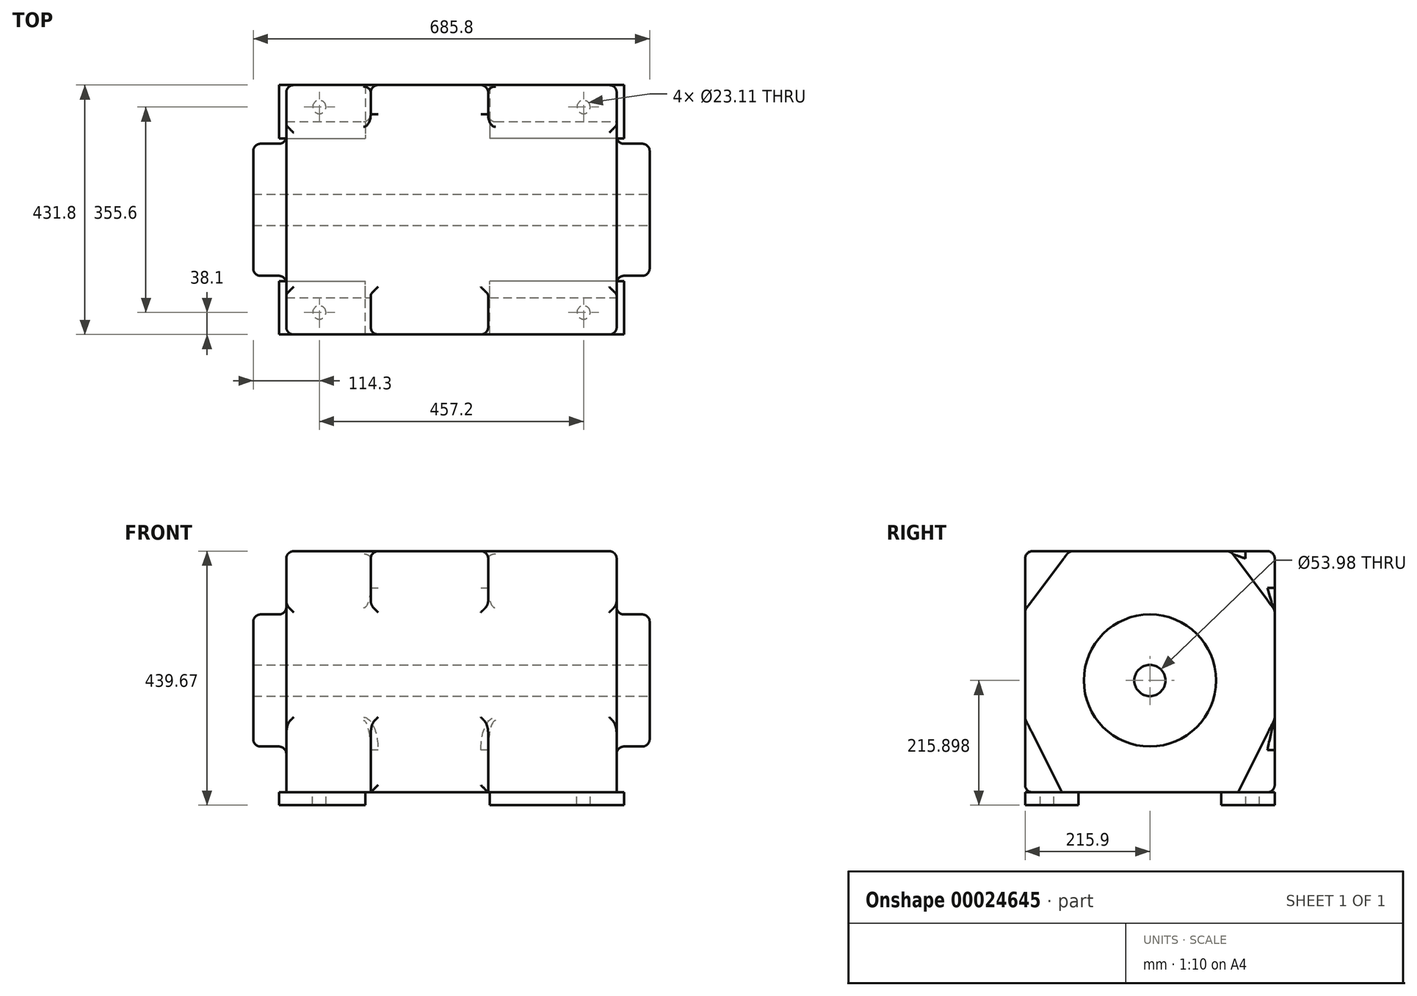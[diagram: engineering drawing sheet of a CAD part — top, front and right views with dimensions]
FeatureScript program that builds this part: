
annotation { "Feature Type Name" : "Feature", "Feature Type Description" : "" }
export const myFeature = defineFeature(function(context is Context, id is Id, definition is map)
    precondition{}
    {
        {
            var Q0;
            Q0=qCreatedBy(makeId("Top.planeOp"),FACE);
            var sketch = newSketch(context, id + "F0", { "sketchPlane" : qUnion([Q0])});
            skLineSegment(sketch, "E0", {"start": v(0, 97.33) * mm, "end": v(0, -215.9) * mm, "construction": true});
            skLineSegment(sketch, "E1", {"start": v(-109.5, 0) * mm, "end": v(101.39, 0) * mm, "construction": true});
            skLineSegment(sketch, "E2.0", {"start": v(-298.45, 215.9) * mm, "end": v(-298.45, -215.9) * mm, "construction": true});
            skLineSegment(sketch, "E3.0", {"start": v(-298.45, -215.9) * mm, "end": v(298.45, -215.9) * mm, "construction": true});
            skLineSegment(sketch, "E4.MirrorCS", {"start": v(298.45, 215.9) * mm, "end": v(298.45, -215.9) * mm, "construction": true});
            skLineSegment(sketch, "E5.MirrorCS", {"start": v(-298.45, 215.9) * mm, "end": v(298.45, 215.9) * mm, "construction": true});
            skPoint(sketch, "E6.orphan", {"position": v(-298.45, 97.33) * mm});
            skPoint(sketch, "E7.orphan", {"position": v(298.45, 97.33) * mm});
            skLineSegment(sketch, "E8.bottom", {"start": v(-298.45, -215.9) * mm, "end": v(-149.1, -215.9) * mm});
            skLineSegment(sketch, "E8.top", {"start": v(-298.45, -123.7) * mm, "end": v(-149.1, -123.7) * mm});
            skLineSegment(sketch, "E8.left", {"start": v(-298.45, -215.9) * mm, "end": v(-298.45, -123.7) * mm});
            skLineSegment(sketch, "E8.right", {"start": v(-149.1, -215.9) * mm, "end": v(-149.1, -123.7) * mm});
            skLineSegment(sketch, "E9.bottom", {"start": v(298.45, -215.9) * mm, "end": v(66.55, -215.9) * mm});
            skLineSegment(sketch, "E9.top", {"start": v(298.45, -123.7) * mm, "end": v(66.55, -123.7) * mm});
            skLineSegment(sketch, "E9.left", {"start": v(298.45, -215.9) * mm, "end": v(298.45, -123.7) * mm});
            skLineSegment(sketch, "E9.right", {"start": v(66.55, -215.9) * mm, "end": v(66.55, -123.7) * mm});
            skLineSegment(sketch, "E10.0", {"start": v(-228.6, 97.33) * mm, "end": v(-228.6, -215.9) * mm, "construction": true});
            skLineSegment(sketch, "E11.0", {"start": v(-228.6, -177.8) * mm, "end": v(101.39, -177.8) * mm, "construction": true});
            skCircle(sketch, "E12", {"center": v(-228.6, -177.8) * mm, "radius": 11.56 * mm});
            skCircle(sketch, "E13.MirrorC", {"center": v(228.6, -177.8) * mm, "radius": 11.56 * mm});
            skCircle(sketch, "E14.MirrorC", {"center": v(-228.6, 177.8) * mm, "radius": 11.56 * mm});
            skLineSegment(sketch, "E15.MirrorCS", {"start": v(-298.45, 123.7) * mm, "end": v(-149.1, 123.7) * mm});
            skLineSegment(sketch, "E16.MirrorCS", {"start": v(-298.45, 215.9) * mm, "end": v(-149.1, 215.9) * mm});
            skLineSegment(sketch, "E17.MirrorCS", {"start": v(-298.45, 215.9) * mm, "end": v(-298.45, 123.7) * mm});
            skLineSegment(sketch, "E18.MirrorCS", {"start": v(-149.1, 215.9) * mm, "end": v(-149.1, 123.7) * mm});
            skLineSegment(sketch, "E19.MirrorCS", {"start": v(298.45, 215.9) * mm, "end": v(298.45, 123.7) * mm});
            skLineSegment(sketch, "E20.MirrorCS", {"start": v(-228.6, 177.8) * mm, "end": v(101.39, 177.8) * mm, "construction": true});
            skLineSegment(sketch, "E21.MirrorCS", {"start": v(-298.45, 215.9) * mm, "end": v(298.45, 215.9) * mm});
            skLineSegment(sketch, "E22.MirrorCS", {"start": v(298.45, 123.7) * mm, "end": v(66.55, 123.7) * mm});
            skCircle(sketch, "E23.MirrorC", {"center": v(228.6, 177.8) * mm, "radius": 11.56 * mm});
            skLineSegment(sketch, "E24.MirrorCS", {"start": v(298.45, 215.9) * mm, "end": v(66.55, 215.9) * mm});
            skLineSegment(sketch, "E25.MirrorCS", {"start": v(66.55, 215.9) * mm, "end": v(66.55, 123.7) * mm});
            skSolve(sketch);
        }
        {
            var Q0;
            Q0=qSketchRegion(id+"F0",true);
            extrude(context, id + "F1", {"entities" : qUnion([Q0]), "oppositeDirection" : true, "depth" : 22.35 * mm});
        }
        {
            var Q0;
            Q0=makeQuery(id+"F1.opExtrude","CAP_FACE",FACE,{"disambiguationData":[OSD([sQuery(id+"F0.wireOp",EDGE,"E14.MirrorC"),sQuery(id+"F0.wireOp",EDGE,"E15.MirrorCS"),sQuery(id+"F0.wireOp",EDGE,"E17.MirrorCS"),sQuery(id+"F0.wireOp",EDGE,"E18.MirrorCS"),sQuery(id+"F0.wireOp",EDGE,"E21.MirrorCS")])],"isStart":true});
            var sketch = newSketch(context, id + "F2", { "sketchPlane" : qUnion([Q0])});
            skLineSegment(sketch, "E26.bottom", {"start": v(-285.75, 139.7) * mm, "end": v(285.75, 139.7) * mm});
            skLineSegment(sketch, "E26.top", {"start": v(-285.75, -139.7) * mm, "end": v(285.75, -139.7) * mm});
            skLineSegment(sketch, "E26.left", {"start": v(-285.75, 139.7) * mm, "end": v(-285.75, -139.7) * mm});
            skLineSegment(sketch, "E26.right", {"start": v(285.75, 139.7) * mm, "end": v(285.75, -139.7) * mm});
            skSolve(sketch);
        }
        {
            var Q0;
            Q0=qSketchRegion(id+"F2",true);
            extrude(context, id + "F3", {"entities" : qUnion([Q0]), "operationType" : NewBodyOperationType.ADD, "depth" : 417.32 * mm});
        }
        {
            var Q0;
            Q0=makeQuery(id+"F3.opExtrude","SWEPT_FACE",FACE,{"disambiguationData":[OSD([sQuery(id+"F2.wireOp",EDGE,"E26.right")])]});
            var sketch = newSketch(context, id + "F4", { "sketchPlane" : qUnion([Q0])});
            skLineSegment(sketch, "E27.0", {"start": v(-215.9, 0) * mm, "end": v(-123.7, 0) * mm, "construction": true});
            skLineSegment(sketch, "E28.0", {"start": v(215.9, 0) * mm, "end": v(123.7, 0) * mm, "construction": true});
            skLineSegment(sketch, "E29.0", {"start": v(139.7, 417.32) * mm, "end": v(-139.7, 417.32) * mm, "construction": true});
            skLineSegment(sketch, "E30", {"start": v(215.9, 0) * mm, "end": v(215.9, 417.32) * mm, "construction": true});
            skLineSegment(sketch, "E31.bottom", {"start": v(0, 0) * mm, "end": v(215.9, 0) * mm});
            skLineSegment(sketch, "E31.top", {"start": v(0, 417.32) * mm, "end": v(139.7, 417.32) * mm});
            skLineSegment(sketch, "E31.left", {"start": v(0, 0) * mm, "end": v(0, 417.32) * mm});
            skLineSegment(sketch, "E31.right", {"start": v(215.9, 127) * mm, "end": v(215.9, 315.72) * mm});
            skLineSegment(sketch, "E32", {"start": v(152.4, 0) * mm, "end": v(215.9, 127) * mm});
            skLineSegment(sketch, "E33", {"start": v(139.7, 417.32) * mm, "end": v(215.9, 315.72) * mm});
            skLineSegment(sketch, "E34.MirrorCS", {"start": v(-215.9, 0) * mm, "end": v(-123.7, 0) * mm});
            skLineSegment(sketch, "E35.MirrorCS", {"start": v(-152.4, 0) * mm, "end": v(-215.9, 127) * mm});
            skLineSegment(sketch, "E36.MirrorCS", {"start": v(0, 417.32) * mm, "end": v(-139.7, 417.32) * mm});
            skLineSegment(sketch, "E37.MirrorCS", {"start": v(0, 0) * mm, "end": v(-215.9, 0) * mm});
            skLineSegment(sketch, "E38.MirrorCS", {"start": v(-215.9, 127) * mm, "end": v(-215.9, 315.72) * mm});
            skLineSegment(sketch, "E39.MirrorCS", {"start": v(-215.9, 127) * mm, "end": v(-215.9, 417.32) * mm});
            skLineSegment(sketch, "E40.MirrorCS", {"start": v(-139.7, 417.32) * mm, "end": v(-215.9, 315.72) * mm});
            skSolve(sketch);
        }
        {
            var Q0;
            Q0=qSketchRegion(id+"F4",true);
            var Q1;
            Q1=makeQuery(id+"F3.opExtrude","SWEPT_FACE",FACE,{"disambiguationData":[OSD([sQuery(id+"F2.wireOp",EDGE,"E26.left")])]});
            extrude(context, id + "F5", {"entities" : qUnion([Q0]), "operationType" : NewBodyOperationType.ADD, "endBound" : BoundingType.UP_TO_SURFACE, "oppositeDirection" : true, "endBoundEntityFace" : qUnion([Q1]), "depth" : 25.4 * mm});
        }
        {
            var Q0;
            Q0=qCreatedBy(makeId("Right.planeOp"),FACE);
            var sketch = newSketch(context, id + "F6", { "sketchPlane" : qUnion([Q0])});
            skLineSegment(sketch, "E41.0", {"start": v(-215.9, 0) * mm, "end": v(-123.7, 0) * mm, "construction": true});
            skLineSegment(sketch, "E42.0", {"start": v(215.9, 0) * mm, "end": v(123.7, 0) * mm, "construction": true});
            skLineSegment(sketch, "E43.bottom", {"start": v(215.9, 0) * mm, "end": v(-215.9, 0) * mm, "construction": true});
            skLineSegment(sketch, "E43.top", {"start": v(215.9, 0) * mm, "end": v(-215.9, 0) * mm, "construction": true});
            skLineSegment(sketch, "E43.left", {"start": v(215.9, 0) * mm, "end": v(215.9, 0) * mm});
            skLineSegment(sketch, "E43.right", {"start": v(-215.9, 0) * mm, "end": v(-215.9, 0) * mm});
            skLineSegment(sketch, "E44.0", {"start": v(139.7, 417.32) * mm, "end": v(-139.7, 417.32) * mm, "construction": true});
            skLineSegment(sketch, "E45", {"start": v(215.9, 0) * mm, "end": v(215.9, 417.32) * mm, "construction": true});
            skLineSegment(sketch, "E46.bottom", {"start": v(215.9, 417.32) * mm, "end": v(-215.9, 417.32) * mm});
            skLineSegment(sketch, "E46.top", {"start": v(215.9, 0) * mm, "end": v(-215.9, 0) * mm});
            skLineSegment(sketch, "E46.left", {"start": v(215.9, 417.32) * mm, "end": v(215.9, 0) * mm});
            skLineSegment(sketch, "E46.right", {"start": v(-215.9, 417.32) * mm, "end": v(-215.9, 0) * mm});
            skSolve(sketch);
        }
        {
            var Q0;
            Q0=makeQuery(id+"F6.imprint","IMPRINT",FACE,{"disambiguationData":[TD([[makeQuery(id+"F6.imprint","IMPRINT",EDGE,{"derivedFrom":sQuery(id+"F6.wireOp",EDGE,"E46.bottom")}),1.0]])]});
            var sketch = newSketch(context, id + "F7", { "sketchPlane" : qUnion([Q0])});
            skSolve(sketch);
        }
        {
            var Q0;
            Q0=qSketchRegion(id+"F7",true);
            var Q1;
            Q1=makeQuery(id+"F6.imprint","IMPRINT",FACE,{"disambiguationData":[TD([[makeQuery(id+"F6.imprint","IMPRINT",EDGE,{"derivedFrom":sQuery(id+"F6.wireOp",EDGE,"E46.bottom")}),1.0]])]});
            var Q2;
            Q2=makeQuery(id+"F1.opExtrude","SWEPT_FACE",FACE,{"disambiguationData":[OSD([sQuery(id+"F0.wireOp",EDGE,"E18.MirrorCS")])]});
            extrude(context, id + "F8", {"entities" : qUnion([Q0, Q1]), "operationType" : NewBodyOperationType.ADD, "oppositeDirection" : true, "endBoundEntityFace" : qUnion([Q2]), "depth" : 139.7 * mm, "hasSecondDirection" : true, "secondDirectionOppositeDirection" : false, "secondDirectionDepth" : 63.5 * mm});
        }
        {
            var Q0;
            Q0=makeQuery(id+"F8.boolean.opBoolean","MERGE",FACE,{"derivedFrom":[makeQuery(id+"F5.opExtrude","SWEPT_FACE",FACE,{"disambiguationData":[OSD([sQuery(id+"F4.wireOp",EDGE,"E31.right")])]}),makeQuery(id+"F8.opExtrude","SWEPT_FACE",FACE,{"disambiguationData":[OSD([sQuery(id+"F6.wireOp",EDGE,"E46.left")])]})]});
            var Q1;
            Q1=makeQuery(id+"F8.boolean.opBoolean","INTERSECT",EDGE,{"derivedFrom":[makeQuery(id+"F5.opExtrude","SWEPT_FACE",FACE,{"disambiguationData":[OSD([sQuery(id+"F4.wireOp",EDGE,"E32")])]}),makeQuery(id+"F8.opExtrude","CAP_FACE",FACE,{"disambiguationData":[OSD([sQuery(id+"F6.wireOp",EDGE,"E46.bottom"),sQuery(id+"F6.wireOp",EDGE,"E46.top"),sQuery(id+"F6.wireOp",EDGE,"E46.left"),sQuery(id+"F6.wireOp",EDGE,"E46.right")])],"isStart":true})]});
            var Q2;
            Q2=makeQuery(id+"F8.boolean.opBoolean","INTERSECT",EDGE,{"derivedFrom":[makeQuery(id+"F5.opExtrude","SWEPT_FACE",FACE,{"disambiguationData":[OSD([sQuery(id+"F4.wireOp",EDGE,"E33")])]}),makeQuery(id+"F8.opExtrude","CAP_FACE",FACE,{"disambiguationData":[OSD([sQuery(id+"F6.wireOp",EDGE,"E46.bottom"),sQuery(id+"F6.wireOp",EDGE,"E46.top"),sQuery(id+"F6.wireOp",EDGE,"E46.left"),sQuery(id+"F6.wireOp",EDGE,"E46.right")])],"isStart":true})]});
            var Q3;
            Q3=makeQuery(id+"F8.boolean.opBoolean","INTERSECT",EDGE,{"derivedFrom":[makeQuery(id+"F5.opExtrude","SWEPT_FACE",FACE,{"disambiguationData":[OSD([sQuery(id+"F4.wireOp",EDGE,"E32")])]}),makeQuery(id+"F8.opExtrude","CAP_FACE",FACE,{"disambiguationData":[OSD([sQuery(id+"F6.wireOp",EDGE,"E46.bottom"),sQuery(id+"F6.wireOp",EDGE,"E46.top"),sQuery(id+"F6.wireOp",EDGE,"E46.left"),sQuery(id+"F6.wireOp",EDGE,"E46.right")])],"isStart":false})]});
            var Q4;
            Q4=makeQuery(id+"F8.boolean.opBoolean","INTERSECT",EDGE,{"derivedFrom":[makeQuery(id+"F5.opExtrude","SWEPT_FACE",FACE,{"disambiguationData":[OSD([sQuery(id+"F4.wireOp",EDGE,"E33")])]}),makeQuery(id+"F8.opExtrude","CAP_FACE",FACE,{"disambiguationData":[OSD([sQuery(id+"F6.wireOp",EDGE,"E46.bottom"),sQuery(id+"F6.wireOp",EDGE,"E46.top"),sQuery(id+"F6.wireOp",EDGE,"E46.left"),sQuery(id+"F6.wireOp",EDGE,"E46.right")])],"isStart":false})]});
            var Q5;
            Q5=makeQuery(id+"F8.boolean.opBoolean","MERGE",FACE,{"derivedFrom":[makeQuery(id+"F5.opExtrude","SWEPT_FACE",FACE,{"disambiguationData":[OSD([sQuery(id+"F4.wireOp",EDGE,"E39.MirrorCS")])]}),makeQuery(id+"F8.opExtrude","SWEPT_FACE",FACE,{"disambiguationData":[OSD([sQuery(id+"F6.wireOp",EDGE,"E46.right")])]})]});
            fillet(context, id + "F9", {"entities" : qUnion([Q0, Q1, Q2, Q3, Q4, Q5]), "radius" : 12.7 * mm, "tangentPropagation" : true, "allowEdgeOverflow" : false});
        }
        {
            var Q0;
            Q0=makeQuery(id+"F8.boolean.opBoolean","MERGE",FACE,{"derivedFrom":[makeQuery(id+"F3.opExtrude","CAP_FACE",FACE,{"disambiguationData":[OSD([sQuery(id+"F2.wireOp",EDGE,"E26.bottom"),sQuery(id+"F2.wireOp",EDGE,"E26.top"),sQuery(id+"F2.wireOp",EDGE,"E26.left"),sQuery(id+"F2.wireOp",EDGE,"E26.right")])],"isStart":false}),makeQuery(id+"F8.opExtrude","SWEPT_FACE",FACE,{"disambiguationData":[OSD([sQuery(id+"F6.wireOp",EDGE,"E46.bottom")])]})]});
            fillet(context, id + "F10", {"entities" : qUnion([Q0]), "radius" : 12.7 * mm, "tangentPropagation" : true, "allowEdgeOverflow" : false});
        }
        {
            var Q0;
            Q0=makeQuery(id+"F7.imprint","IMPRINT",FACE,{"disambiguationData":[TD([[makeQuery(id+"F7.imprint","IMPRINT",EDGE,{"derivedFrom":makeQuery(id+"F6.imprint","IMPRINT",EDGE,{"derivedFrom":sQuery(id+"F6.wireOp",EDGE,"E46.bottom")})}),1.0]])]});
            var sketch = newSketch(context, id + "F11", { "sketchPlane" : qUnion([Q0])});
            skLineSegment(sketch, "E47.0", {"start": v(-215.9, -22.35) * mm, "end": v(-123.7, -22.35) * mm, "construction": true});
            skLineSegment(sketch, "E48.0", {"start": v(-215.9, 193.55) * mm, "end": v(0, 193.55) * mm, "construction": true});
            skLineSegment(sketch, "E49", {"start": v(0, 0) * mm, "end": v(0, 468.14) * mm, "construction": true});
            skCircle(sketch, "E50", {"center": v(0, 193.55) * mm, "radius": 114.3 * mm});
            skSolve(sketch);
        }
        {
            var Q0;
            Q0=qSketchRegion(id+"F11",true);
            extrude(context, id + "F12", {"entities" : qUnion([Q0]), "operationType" : NewBodyOperationType.ADD, "depth" : 342.9 * mm, "hasSecondDirection" : true, "secondDirectionOppositeDirection" : true, "secondDirectionDepth" : 342.9 * mm});
        }
        {
            var Q0;
            Q0=makeQuery(id+"F12.boolean.opBoolean","INTERSECT",EDGE,{"derivedFrom":[makeQuery(id+"F5.boolean.opBoolean","MERGE",FACE,{"derivedFrom":[makeQuery(id+"F3.opExtrude","SWEPT_FACE",FACE,{"disambiguationData":[OSD([sQuery(id+"F2.wireOp",EDGE,"E26.right")])]}),makeQuery(id+"F5.opExtrude","CAP_FACE",FACE,{"disambiguationData":[OSD([sQuery(id+"F4.wireOp",EDGE,"E31.bottom"),sQuery(id+"F4.wireOp",EDGE,"E31.top"),sQuery(id+"F4.wireOp",EDGE,"E31.right"),sQuery(id+"F4.wireOp",EDGE,"E32"),sQuery(id+"F4.wireOp",EDGE,"E33"),sQuery(id+"F4.wireOp",EDGE,"E35.MirrorCS"),sQuery(id+"F4.wireOp",EDGE,"E36.MirrorCS"),sQuery(id+"F4.wireOp",EDGE,"E37.MirrorCS"),sQuery(id+"F4.wireOp",EDGE,"E39.MirrorCS"),sQuery(id+"F4.wireOp",EDGE,"E40.MirrorCS")])],"isStart":true})]}),makeQuery(id+"F12.opExtrude","SWEPT_FACE",FACE,{"disambiguationData":[OSD([sQuery(id+"F11.wireOp",EDGE,"E50")])]})]});
            var Q1;
            Q1=makeQuery(id+"F12.opExtrude","CAP_EDGE",EDGE,{"disambiguationData":[OSD([sQuery(id+"F11.wireOp",EDGE,"E50")])],"isStart":false});
            var Q2;
            Q2=makeQuery(id+"F12.opExtrude","CAP_FACE",FACE,{"disambiguationData":[OSD([sQuery(id+"F11.wireOp",EDGE,"E50")])],"isStart":true});
            var Q3;
            Q3=makeQuery(id+"F12.boolean.opBoolean","INTERSECT",EDGE,{"derivedFrom":[makeQuery(id+"F5.boolean.opBoolean","MERGE",FACE,{"derivedFrom":[makeQuery(id+"F3.opExtrude","SWEPT_FACE",FACE,{"disambiguationData":[OSD([sQuery(id+"F2.wireOp",EDGE,"E26.left")])]}),makeQuery(id+"F5.opExtrude","CAP_FACE",FACE,{"disambiguationData":[OSD([sQuery(id+"F4.wireOp",EDGE,"E31.bottom"),sQuery(id+"F4.wireOp",EDGE,"E31.top"),sQuery(id+"F4.wireOp",EDGE,"E31.right"),sQuery(id+"F4.wireOp",EDGE,"E32"),sQuery(id+"F4.wireOp",EDGE,"E33"),sQuery(id+"F4.wireOp",EDGE,"E35.MirrorCS"),sQuery(id+"F4.wireOp",EDGE,"E36.MirrorCS"),sQuery(id+"F4.wireOp",EDGE,"E37.MirrorCS"),sQuery(id+"F4.wireOp",EDGE,"E39.MirrorCS"),sQuery(id+"F4.wireOp",EDGE,"E40.MirrorCS")])],"isStart":false})]}),makeQuery(id+"F12.opExtrude","SWEPT_FACE",FACE,{"disambiguationData":[OSD([sQuery(id+"F11.wireOp",EDGE,"E50")])]})]});
            fillet(context, id + "F13", {"entities" : qUnion([Q0, Q1, Q2, Q3]), "radius" : 12.7 * mm, "tangentPropagation" : true, "allowEdgeOverflow" : false});
        }
        {
            var Q0;
            Q0=makeQuery(id+"F12.opExtrude","CAP_FACE",FACE,{"disambiguationData":[OSD([sQuery(id+"F11.wireOp",EDGE,"E50")])],"isStart":false});
            var sketch = newSketch(context, id + "F14", { "sketchPlane" : qUnion([Q0])});
            skCircle(sketch, "E51.0.0", {"center": v(0, 193.55) * mm, "radius": 101.6 * mm, "construction": true});
            skCircle(sketch, "E52", {"center": v(0, 193.55) * mm, "radius": 26.99 * mm});
            skSolve(sketch);
        }
        {
            var Q0;
            Q0=qSketchRegion(id+"F14",true);
            extrude(context, id + "F15", {"entities" : qUnion([Q0]), "operationType" : NewBodyOperationType.REMOVE, "endBound" : BoundingType.THROUGH_ALL, "oppositeDirection" : true, "depth" : 25.4 * mm});
        }
    });
